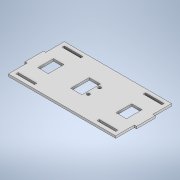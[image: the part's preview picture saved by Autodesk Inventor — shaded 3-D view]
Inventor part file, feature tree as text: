
AUTODESK INVENTOR PART (.ipt)
format: ipt  version: 2020 (Build 240168000, 168)  size: 200,704 bytes
history: native  units: in
note: dims shown in document units (in); Inventor stores cm internally (conversion verified against a paired STEP export)
features: extrude x6, sketch x6
ambient origin geometry x8: Origin, YZ Plane, XZ Plane, XY Plane, X Axis, Y Axis, Z Axis, Center Point
bodies: Solid1 (feature_tree)
feature tree (12):
  extrude  "Extrusion1"  Depth=1.1811in TaperAngle=0.0deg
  extrude  "Extrusion2"  Depth=0.8268in
  extrude  "Extrusion3"  Depth=0.5906in
  extrude  "Extrusion4"  Depth=0.1575in
  extrude  "Extrusion5"  Depth=0.8268in
  extrude  "Extrusion6"  Depth=0.5906in
  sketch  "Sketch1"  dims[d9=0.1181in d10=0.0in d30=1.1811in d31=0.0in]
  sketch  "Sketch2"  dims[d56=0.5512in d57=0.8268in]
  sketch  "Sketch3"  dims[d59=0.9843in d60=0.5906in]
  sketch  "Sketch4"  dims[d61=0.1575in d62=0.1575in]
  sketch  "Sketch5"  dims[d63=0.5512in d64=0.8268in]
  sketch  "Sketch6"  dims[d65=0.3937in d66=0.0in d67=0.5906in d68=0.5906in d69=0.3937in d70=0.0in d79=0.0055in d80=0.0in d81=0.0055in d82=0.0in]
